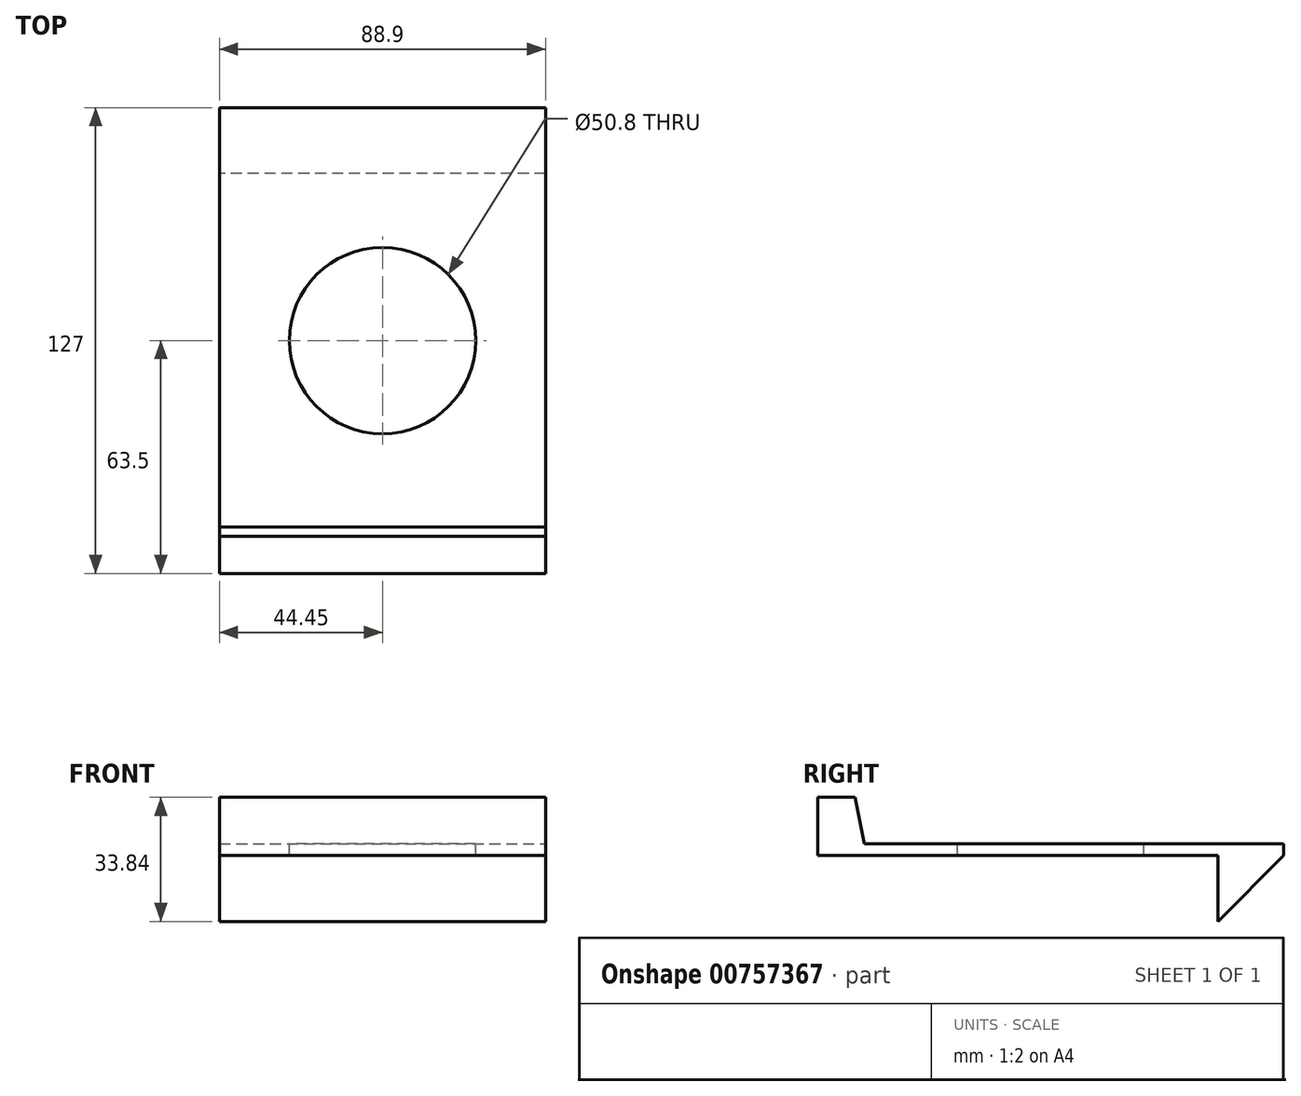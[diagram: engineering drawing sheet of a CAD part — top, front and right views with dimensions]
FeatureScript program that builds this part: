
annotation { "Feature Type Name" : "Feature", "Feature Type Description" : "" }
export const myFeature = defineFeature(function(context is Context, id is Id, definition is map)
    precondition{}
    {
        {
            var Q0;
            Q0=qCreatedBy(makeId("Top.planeOp"),FACE);
            var sketch = newSketch(context, id + "F0", { "sketchPlane" : qUnion([Q0])});
            skLineSegment(sketch, "E0.bottom", {"start": v(-44.45, -63.5) * mm, "end": v(44.45, -63.5) * mm});
            skLineSegment(sketch, "E0.top", {"start": v(-44.45, 63.5) * mm, "end": v(44.45, 63.5) * mm});
            skLineSegment(sketch, "E0.left", {"start": v(-44.45, -63.5) * mm, "end": v(-44.45, 63.5) * mm});
            skLineSegment(sketch, "E0.right", {"start": v(44.45, -63.5) * mm, "end": v(44.45, 63.5) * mm});
            skPoint(sketch, "E0.middle", {"position": v(0, 0) * mm});
            skSolve(sketch);
        }
        {
            var Q0;
            Q0 = qSketchRegion(id + "F0", true);
            extrude(context, id + "F1", {"entities" : qUnion([Q0]), "depth" : 3.17 * mm, "offsetDistance" : 25.4 * mm});
        }
        {
            var Q0;
            Q0=makeQuery(id+"F1.opExtrude","CAP_FACE",FACE,{"disambiguationData":[OSD([sQuery(id+"F0.wireOp",EDGE,"E0.bottom"),sQuery(id+"F0.wireOp",EDGE,"E0.top"),sQuery(id+"F0.wireOp",EDGE,"E0.left"),sQuery(id+"F0.wireOp",EDGE,"E0.right")])],"isStart":true});
            var sketch = newSketch(context, id + "F2", { "sketchPlane" : qUnion([Q0])});
            skLineSegment(sketch, "E1", {"start": v(44.45, -63.5) * mm, "end": v(44.45, -45.54) * mm});
            skLineSegment(sketch, "E2", {"start": v(44.45, -45.54) * mm, "end": v(-44.45, -45.54) * mm});
            skSolve(sketch);
        }
        {
            var Q0;
            Q0 = qSketchRegion(id + "F2", true);
            var Q1;
            Q1=makeQuery(id+"F2.imprint","IMPRINT",FACE,{"disambiguationData":[TD([[makeQuery(id+"F2.imprint","IMPRINT",EDGE,{"derivedFrom":sQuery(id+"F2.wireOp",EDGE,"E1")}),-1.0]])]});
            extrude(context, id + "F3", {"entities" : qUnion([Q0, Q1]), "operationType" : NewBodyOperationType.ADD, "depth" : 17.96 * mm, "offsetDistance" : 25.4 * mm});
        }
        {
            var Q0;
            Q0=makeQuery(id+"F3.opExtrude","CAP_EDGE",EDGE,{"disambiguationData":[OSD([sQuery(id+"F0.wireOp",EDGE,"E0.top")])],"isStart":false});
            chamfer(context, id + "F4", {"entities" : qUnion([Q0]), "width" : 17.96 * mm, "tangentPropagation" : true});
        }
        {
            var Q0;
            Q0=makeQuery(id+"F1.opExtrude","CAP_FACE",FACE,{"disambiguationData":[OSD([sQuery(id+"F0.wireOp",EDGE,"E0.bottom"),sQuery(id+"F0.wireOp",EDGE,"E0.top"),sQuery(id+"F0.wireOp",EDGE,"E0.left"),sQuery(id+"F0.wireOp",EDGE,"E0.right")])],"isStart":false});
            var sketch = newSketch(context, id + "F5", { "sketchPlane" : qUnion([Q0])});
            skCircle(sketch, "E3", {"center": v(0, 0) * mm, "radius": 25.4 * mm});
            skSolve(sketch);
        }
        {
            var Q0;
            Q0 = qSketchRegion(id + "F5", true);
            extrude(context, id + "F6", {"entities" : qUnion([Q0]), "operationType" : NewBodyOperationType.REMOVE, "oppositeDirection" : true, "depth" : 3.17 * mm, "offsetDistance" : 25.4 * mm});
        }
        {
            var Q0;
            Q0=makeQuery(id+"F1.opExtrude","CAP_FACE",FACE,{"disambiguationData":[OSD([sQuery(id+"F0.wireOp",EDGE,"E0.bottom"),sQuery(id+"F0.wireOp",EDGE,"E0.top"),sQuery(id+"F0.wireOp",EDGE,"E0.left"),sQuery(id+"F0.wireOp",EDGE,"E0.right")])],"isStart":false});
            var sketch = newSketch(context, id + "F7", { "sketchPlane" : qUnion([Q0])});
            skLineSegment(sketch, "E4", {"start": v(44.45, -63.5) * mm, "end": v(44.45, -50.8) * mm});
            skLineSegment(sketch, "E5", {"start": v(44.45, -50.8) * mm, "end": v(-44.45, -50.8) * mm});
            skSolve(sketch);
        }
        {
            var Q0;
            Q0 = qSketchRegion(id + "F7", true);
            var Q1;
            Q1=makeQuery(id+"F7.imprint","IMPRINT",FACE,{"disambiguationData":[TD([[makeQuery(id+"F7.imprint","IMPRINT",EDGE,{"derivedFrom":sQuery(id+"F7.wireOp",EDGE,"E4")}),1.0]])]});
            extrude(context, id + "F8", {"entities" : qUnion([Q0, Q1]), "operationType" : NewBodyOperationType.ADD, "depth" : 12.7 * mm, "offsetDistance" : 25.4 * mm});
        }
        {
            var Q0;
            Q0=makeQuery(id+"F8.opExtrude","CAP_EDGE",EDGE,{"disambiguationData":[OSD([sQuery(id+"F7.wireOp",EDGE,"E5")])],"isStart":false});
            chamfer(context, id + "F9", {"entities" : qUnion([Q0]), "chamferType" : ChamferType.TWO_OFFSETS, "width1" : 2.54 * mm, "oppositeDirection" : false, "width2" : 12.7 * mm, "tangentPropagation" : true});
        }
    });
